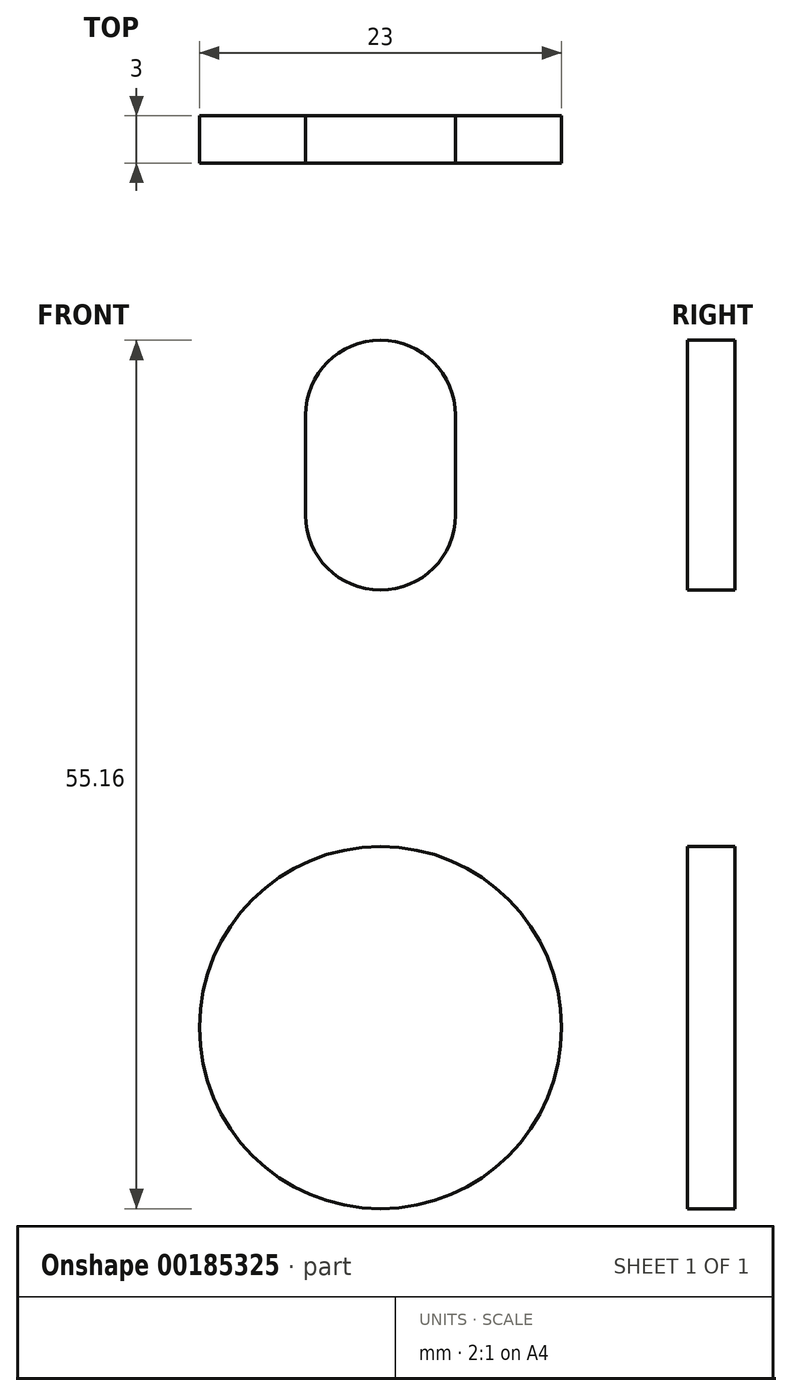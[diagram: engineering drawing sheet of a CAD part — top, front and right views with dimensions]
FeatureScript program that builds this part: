
annotation { "Feature Type Name" : "Feature", "Feature Type Description" : "" }
export const myFeature = defineFeature(function(context is Context, id is Id, definition is map)
    precondition{}
    {
        {
            var Q0;
            Q0=qCreatedBy(makeId("Front.planeOp"),FACE);
            var sketch = newSketch(context, id + "F0", { "sketchPlane" : qUnion([Q0])});
            skCircle(sketch, "E0", {"center": v(0, 0) * mm, "radius": 11.5 * mm});
            skLineSegment(sketch, "E1", {"start": v(0, 0) * mm, "end": v(0, -15) * mm, "construction": true});
            skLineSegment(sketch, "E2", {"start": v(0, -15) * mm, "end": v(24.5, -15) * mm, "construction": true});
            skLineSegment(sketch, "E3", {"start": v(0, -15) * mm, "end": v(-24.5, -15) * mm, "construction": true});
            skLineSegment(sketch, "E4", {"start": v(0, 0) * mm, "end": v(0, 15) * mm, "construction": true});
            skCircle(sketch, "E5", {"center": v(0, 0) * mm, "radius": 26.2 * mm, "construction": true});
            skLineSegment(sketch, "E6", {"start": v(0, 15) * mm, "end": v(0, 15) * mm});
            skCircle(sketch, "E7", {"center": v(-24.5, -15) * mm, "radius": 1.5 * mm, "construction": true});
            skArc(sketch, "E8.trimOffspring", {"start": v(-30.27, 9.6) * mm, "mid": v(-31.38, 4.85) * mm, "end": v(-31.75, 0) * mm});
            skCircle(sketch, "E9", {"center": v(0, 32.55) * mm, "radius": 6.35 * mm, "construction": true});
            skLineSegment(sketch, "E10", {"start": v(0, 32.55) * mm, "end": v(0, 38.9) * mm, "construction": true});
            skCircle(sketch, "E11", {"center": v(0, 38.9) * mm, "radius": 12.7 * mm, "construction": true});
            skArc(sketch, "E12", {"start": v(-4.76, 32.55) * mm, "mid": v(0, 27.79) * mm, "end": v(4.76, 32.55) * mm});
            skArc(sketch, "E13", {"start": v(4.76, 38.9) * mm, "mid": v(0, 43.66) * mm, "end": v(-4.76, 38.9) * mm});
            skLineSegment(sketch, "E14", {"start": v(4.76, 38.9) * mm, "end": v(4.76, 32.55) * mm});
            skLineSegment(sketch, "E15", {"start": v(-4.76, 38.9) * mm, "end": v(-4.76, 32.55) * mm});
            skArc(sketch, "E16", {"start": v(19.07, 44.94) * mm, "mid": v(0, 58.9) * mm, "end": v(-19.07, 44.94) * mm});
            skLineSegment(sketch, "E17", {"start": v(-19.07, 44.94) * mm, "end": v(-30.27, 9.6) * mm});
            skLineSegment(sketch, "E18", {"start": v(-31.75, 0) * mm, "end": v(-31.75, -6.35) * mm});
            skLineSegment(sketch, "E19", {"start": v(6.35, -31.75) * mm, "end": v(-6.35, -31.75) * mm});
            skPoint(sketch, "E20.visualSharp", {"position": v(-31.75, -31.75) * mm});
            skArc(sketch, "E20.filletArc", {"start": v(-31.75, -6.35) * mm, "mid": v(-24.31, -24.31) * mm, "end": v(-6.35, -31.75) * mm});
            skPoint(sketch, "E21.visualSharp", {"position": v(31.75, -31.75) * mm});
            skArc(sketch, "E21.filletArc", {"start": v(6.35, -31.75) * mm, "mid": v(24.31, -24.31) * mm, "end": v(31.75, -6.35) * mm});
            skLineSegment(sketch, "E22", {"start": v(31.75, -6.35) * mm, "end": v(31.75, 40.32) * mm});
            skSolve(sketch);
        }
        {
            var Q0;
            Q0 = qSketchRegion(id + "F0", true);
            extrude(context, id + "F1", {"entities" : qUnion([Q0]), "depth" : 3 * mm});
        }
        {
            var Q0;
            Q0=makeQuery(id+"F1.opExtrude","CAP_FACE",FACE,{"disambiguationData":[OSD([sQuery(id+"F0.wireOp",EDGE,"E0"),sQuery(id+"F0.wireOp",EDGE,"y5h0sFBt-dmta-BE1Y-Fk98-uDJHR25TXx4M"),sQuery(id+"F0.wireOp",EDGE,"m19ymkv9-wd0l-0s28-hNZn-R9RvO0SvdrBT"),sQuery(id+"F0.wireOp",EDGE,"O0nAMlKG-x8OG-ZuM1-MwK0-6rFEJpRCGgqf"),sQuery(id+"F0.wireOp",EDGE,"500ba1a6-724b-4476-b7a4-126c5525648e.trimOffspring"),sQuery(id+"F0.wireOp",EDGE,"E8.trimOffspring"),sQuery(id+"F0.wireOp",EDGE,"E12"),sQuery(id+"F0.wireOp",EDGE,"E13"),sQuery(id+"F0.wireOp",EDGE,"E14"),sQuery(id+"F0.wireOp",EDGE,"E15"),sQuery(id+"F0.wireOp",EDGE,"E16"),sQuery(id+"F0.wireOp",EDGE,"E17"),sQuery(id+"F0.wireOp",EDGE,"Mc9cg8k3-ZOso-3P51-RLvI-5hbRm2KPsArD")])],"isStart":false});
            var sketch = newSketch(context, id + "F2", { "sketchPlane" : qUnion([Q0])});
            skLineSegment(sketch, "E23", {"start": v(0, 38.45) * mm, "end": v(-12.5, 38.45) * mm, "construction": true});
            skLineSegment(sketch, "E24", {"start": v(0, 38.45) * mm, "end": v(12.5, 38.45) * mm, "construction": true});
            skLineSegment(sketch, "E25", {"start": v(0, 32.55) * mm, "end": v(12.5, 32.55) * mm, "construction": true});
            skLineSegment(sketch, "E26", {"start": v(0, 32.55) * mm, "end": v(-12.5, 32.55) * mm, "construction": true});
            skLineSegment(sketch, "E27", {"start": v(-10.91, 38.45) * mm, "end": v(-10.91, 32.55) * mm});
            skLineSegment(sketch, "E28", {"start": v(10.91, 38.45) * mm, "end": v(10.91, 32.55) * mm});
            skArc(sketch, "E29", {"start": v(-10.91, 38.45) * mm, "mid": v(-12.5, 40.04) * mm, "end": v(-14.09, 38.45) * mm});
            skArc(sketch, "E30", {"start": v(-10.91, 32.55) * mm, "mid": v(-12.5, 30.96) * mm, "end": v(-14.09, 32.55) * mm});
            skArc(sketch, "E31", {"start": v(10.91, 38.45) * mm, "mid": v(12.5, 40.04) * mm, "end": v(14.09, 38.45) * mm});
            skArc(sketch, "E32", {"start": v(10.91, 32.55) * mm, "mid": v(12.5, 30.96) * mm, "end": v(14.09, 32.55) * mm});
            skLineSegment(sketch, "E33", {"start": v(-14.09, 38.45) * mm, "end": v(-14.09, 32.55) * mm});
            skLineSegment(sketch, "E34", {"start": v(14.09, 38.45) * mm, "end": v(14.09, 32.55) * mm});
            skSolve(sketch);
        }
        {
            var Q0;
            Q0 = qSketchRegion(id + "F2", true);
            extrude(context, id + "F3", {"entities" : qUnion([Q0]), "operationType" : NewBodyOperationType.REMOVE, "endBound" : BoundingType.THROUGH_ALL, "oppositeDirection" : true, "depth" : 25.4 * mm});
        }
        {
            var Q0;
            Q0=makeQuery(id+"F1.opExtrude","CAP_FACE",FACE,{"disambiguationData":[OSD([sQuery(id+"F0.wireOp",EDGE,"E0"),sQuery(id+"F0.wireOp",EDGE,"y5h0sFBt-dmta-BE1Y-Fk98-uDJHR25TXx4M"),sQuery(id+"F0.wireOp",EDGE,"m19ymkv9-wd0l-0s28-hNZn-R9RvO0SvdrBT"),sQuery(id+"F0.wireOp",EDGE,"O0nAMlKG-x8OG-ZuM1-MwK0-6rFEJpRCGgqf"),sQuery(id+"F0.wireOp",EDGE,"500ba1a6-724b-4476-b7a4-126c5525648e.trimOffspring"),sQuery(id+"F0.wireOp",EDGE,"E8.trimOffspring"),sQuery(id+"F0.wireOp",EDGE,"E12"),sQuery(id+"F0.wireOp",EDGE,"E13"),sQuery(id+"F0.wireOp",EDGE,"E14"),sQuery(id+"F0.wireOp",EDGE,"E15"),sQuery(id+"F0.wireOp",EDGE,"E16"),sQuery(id+"F0.wireOp",EDGE,"E17"),sQuery(id+"F0.wireOp",EDGE,"Mc9cg8k3-ZOso-3P51-RLvI-5hbRm2KPsArD")])],"isStart":false});
            var sketch = newSketch(context, id + "F4", { "sketchPlane" : qUnion([Q0])});
            skCircle(sketch, "E35", {"center": v(0, 15) * mm, "radius": 1.25 * mm});
            skCircle(sketch, "E36", {"center": v(-24.5, -15) * mm, "radius": 1.25 * mm});
            skCircle(sketch, "E37", {"center": v(24.5, -15) * mm, "radius": 1.25 * mm});
            skSolve(sketch);
        }
        {
            var Q0;
            Q0 = qSketchRegion(id + "F4", true);
            extrude(context, id + "F5", {"entities" : qUnion([Q0]), "operationType" : NewBodyOperationType.REMOVE, "endBound" : BoundingType.THROUGH_ALL, "oppositeDirection" : true, "depth" : 25.4 * mm});
        }
    });
